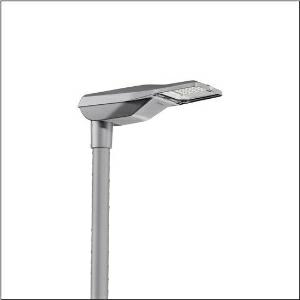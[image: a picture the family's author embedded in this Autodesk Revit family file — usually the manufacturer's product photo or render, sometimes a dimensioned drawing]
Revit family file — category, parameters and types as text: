
# Revit family: streetlight_sl_21_iq_micro___st1_5a_5xe1p31g08cb_4914
name_source: partatom
category: Lighting Fixtures
units: mm (PartAtom-declared; Revit-internal decimal feet)

## family parameters
Cut with Voids When Loaded = No
Host = Face
Light Source = No
Part Type = Normal
Room Calculation Point = No
Round Connector Dimension = Use Diameter
Shared = No

## types (1)
- --- (1 x LED, 2820 lm, 19.4 W, 3000K)
    Apparent Load = 19 VA
    CIE Flux Codes = 22 53 95 100 100
    Color Rendering = 70
    Color Temperature = 3000K
    Default Elevation = 1800 mm
    Description = Streetlight SL 21 iQ micro, mast luminaire, primary light control with lens, of PMMA, primary optical cover: cover, of toughened safety glass, transparent, light distribution: ST1.5a, light emission: direct distribution, primary light characteristic: asymmetric, installation type: post-top, side-entry, LED, High Power LED, rated luminous flux: 2.820lm, luminous efficacy: 145lm/W, light colour: 730, colour temperature: 3000K, control gear: iQ Street-Remote, control: Street-Remote, Auto-Match, Temp-Guard, Lumen-Switch, Night-Set, Smart-Wire, Light-Fading, Desk-Remote (wireless, voltage-free reading and setting of iQ features in the workshop via application-optimized NFC function/RFID function), optimised constant luminous flux control (CLO 2.0), pre-setting: linear dimming characteristic, mains connection: 220..240V, AC, 50/60Hz, start of lifetime: 19W, end of service life: 20W, reduction: 10W, luminaire housing, of diecast aluminium, powder-coated, SITECO metallic grey (DB 702S), corrosivity category C5 high according to DIN EN ISO 12944, please order mast flange separately, inclination adjustable: 0°, 5°, 10°, 15°, sealing non-destructively replaceable, multi-level sealing system, length: 528mm, width: 235mm, height: 110mm, mast flange for spigot size: 42mm (side-entry): 5XC10008XM4, 60/48mm (side-entry/post-top): 5XC10108XM2, 76/60mm (side-entry/post-top): 5XC10108XM1, protection rating (complete): IP66, insulation class (complete): insulation class II (safety insulation), certification: CE, ENEC, ENEC+, VDE, impact resistance: IK10, permissible operating ambient temperature for outdoor applications: -40..+50°C, standard-compliant lighting for roads and squares, packaging unit: 1 piece

Light Distribution: ST1.5a
    Height = 110 mm
    Lamp = 1 x LED
    Lamp Light Flux = 2820 lm
    Lamp Power = 19.4 W
    Lamp count = 1
    Length = 528 mm
    Luminous efficacy = 145 lm/W
    Manufacturer = Siteco
    ModVariant = No
    Model = 5XE1P31G08CB
    Number of Poles = 1
    OnlyDefault = Yes
    Power Factor = 1
    Product Name = Streetlight SL 21 iQ micro | ST1.5a
    Product group = mast luminaire | pylon top
    ProductGroupID = 6100
    Protection Class = Protection class II
    Protection Degree = IP 66
    RLX_Detail_Level = 1
    RLX_Emergency_Light_Flux = 0 lm
    RLX_Emergency_Type = 0
    RLX_Emergency_Type_DB = No
    RlxData = <blob elided: 102265 chars, md5=1b949d00>
    Socket = socket
    Standby Power = 0 W
    System Light Flux = 2820 lm
    System Power = 19 W
    Type Comments = factory setting: luminous flux: 100 % | dim-lin: 254 | 387 mA
    Type Image = l_1006881.jpg
    URL = http://relux.com
    VarID = @adj_137567
    Voltage = 0 V
    Weight = 0.00 kg
    Width = 235 mm

## geometry (parser evidence)
native form markers: Blend x4, Sweep x11
no freeform markers — native parametric forms only
